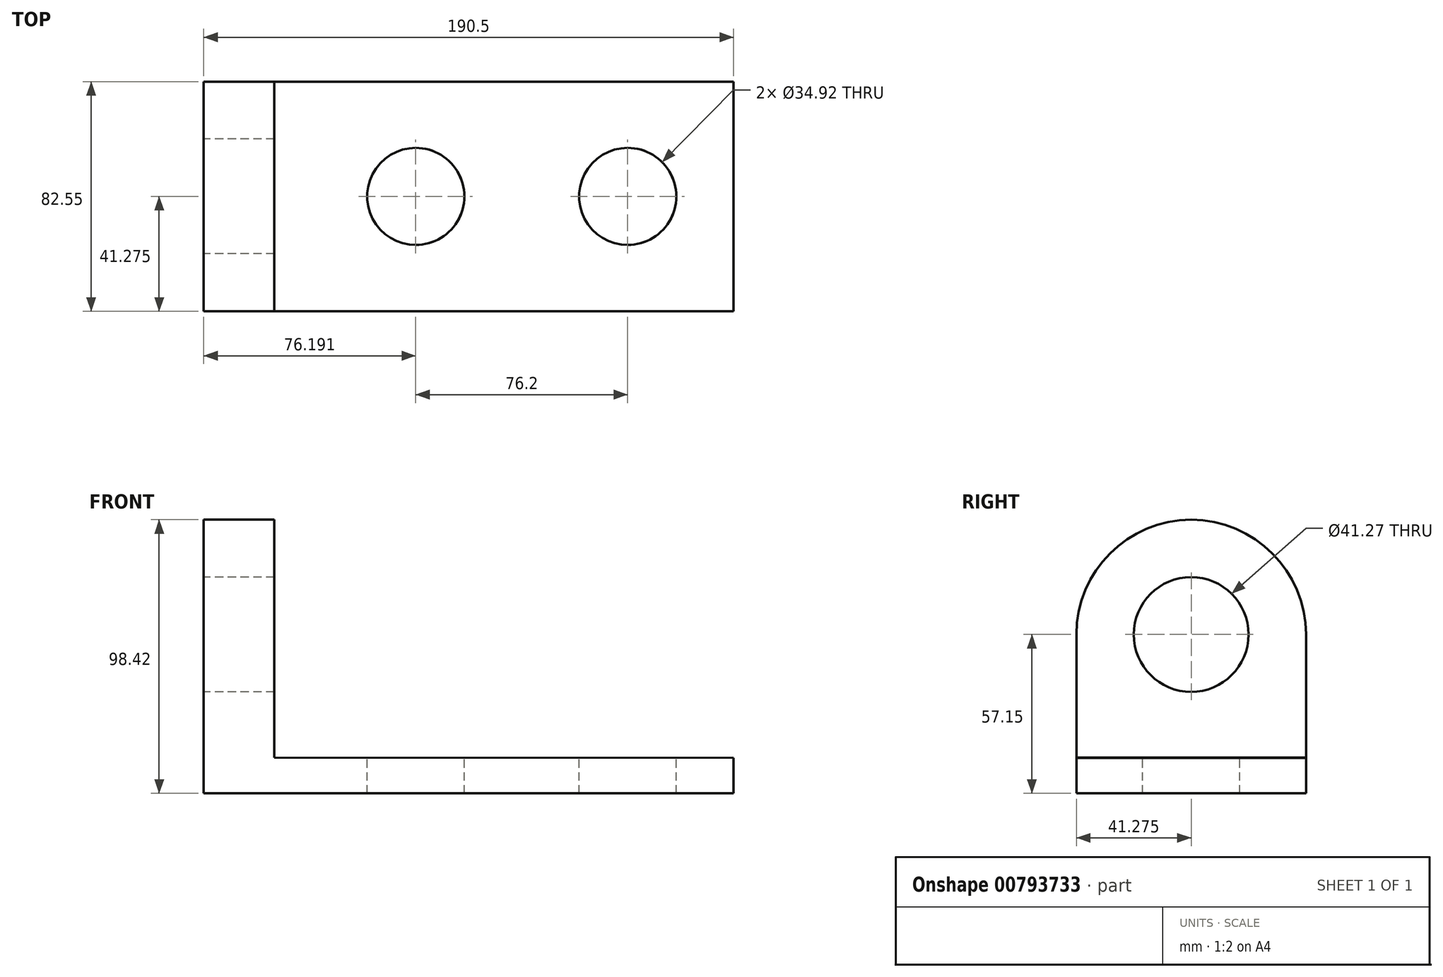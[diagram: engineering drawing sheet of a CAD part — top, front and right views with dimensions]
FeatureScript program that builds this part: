
annotation { "Feature Type Name" : "Feature", "Feature Type Description" : "" }
export const myFeature = defineFeature(function(context is Context, id is Id, definition is map)
    precondition{}
    {
        {
            var Q0;
            Q0=qCreatedBy(makeId("Front.planeOp"),FACE);
            var sketch = newSketch(context, id + "F0", { "sketchPlane" : qUnion([Q0])});
            skLineSegment(sketch, "E0", {"start": v(0, 0) * mm, "end": v(190.5, 0) * mm});
            skLineSegment(sketch, "E1", {"start": v(190.5, 0) * mm, "end": v(190.5, 12.7) * mm});
            skLineSegment(sketch, "E2", {"start": v(0, 0) * mm, "end": v(0, 114.3) * mm});
            skLineSegment(sketch, "E3", {"start": v(0, 114.3) * mm, "end": v(25.4, 114.3) * mm});
            skLineSegment(sketch, "E4", {"start": v(25.4, 114.3) * mm, "end": v(25.4, 12.92) * mm});
            skLineSegment(sketch, "E5", {"start": v(25.4, 12.92) * mm, "end": v(190.5, 12.7) * mm});
            skSolve(sketch);
        }
        {
            var Q0;
            Q0=makeQuery(id+"F0.imprint","IMPRINT",FACE,{"disambiguationData":[TD([[makeQuery(id+"F0.imprint","IMPRINT",EDGE,{"derivedFrom":sQuery(id+"F0.wireOp",EDGE,"E0")}),1.0]])]});
            extrude(context, id + "F1", {"entities" : qUnion([Q0]), "depth" : 82.55 * mm, "offsetDistance" : 25.4 * mm});
        }
        {
            var Q0;
            Q0=makeQuery(id+"F1.opExtrude","SWEPT_FACE",FACE,{"disambiguationData":[OSD([sQuery(id+"F0.wireOp",EDGE,"E2")])]});
            var sketch = newSketch(context, id + "F2", { "sketchPlane" : qUnion([Q0])});
            skLineSegment(sketch, "E6", {"start": v(0, 0) * mm, "end": v(0, 57.15) * mm});
            skLineSegment(sketch, "E7", {"start": v(82.55, 0) * mm, "end": v(82.55, 57.15) * mm});
            skArc(sketch, "E8", {"start": v(82.55, 57.15) * mm, "mid": v(41.27, 98.43) * mm, "end": v(0, 57.15) * mm});
            skCircle(sketch, "E9", {"center": v(41.27, 57.15) * mm, "radius": 20.64 * mm});
            skSolve(sketch);
        }
        {
            var Q0;
            Q0=makeQuery(id+"F2.imprint","IMPRINT",FACE,{"disambiguationData":[TD([[makeQuery(id+"F2.imprint","IMPRINT",EDGE,{"derivedFrom":sQuery(id+"F2.wireOp",EDGE,"E9")}),1.0]])]});
            var Q1;
            {var subQ0=sQuery(id+"F2.wireOp",EDGE,"E8");Q1=makeQuery(id+"F2.imprint","IMPRINT",FACE,{"disambiguationData":[TD([[makeQuery(id+"F2.imprint","IMPRINT",EDGE,{"derivedFrom":subQ0}),-1.0]])]});}
            extrude(context, id + "F3", {"entities" : qUnion([Q0, Q1]), "operationType" : NewBodyOperationType.REMOVE, "oppositeDirection" : true, "depth" : 152.4 * mm, "offsetDistance" : 25.4 * mm});
        }
        {
            var Q0;
            Q0=makeQuery(id+"F1.opExtrude","SWEPT_FACE",FACE,{"disambiguationData":[OSD([sQuery(id+"F0.wireOp",EDGE,"E5")])]});
            var sketch = newSketch(context, id + "F4", { "sketchPlane" : qUnion([Q0])});
            skLineSegment(sketch, "E10", {"start": v(190.48, -41.28) * mm, "end": v(152.38, -41.28) * mm, "construction": true});
            skLineSegment(sketch, "E11", {"start": v(152.38, -41.28) * mm, "end": v(76.18, -41.28) * mm, "construction": true});
            skCircle(sketch, "E12", {"center": v(76.18, -41.28) * mm, "radius": 17.46 * mm});
            skCircle(sketch, "E13", {"center": v(152.38, -41.28) * mm, "radius": 17.46 * mm});
            skSolve(sketch);
        }
        {
            var Q0;
            Q0=qSketchRegion(id+"F4",true);
            extrude(context, id + "F5", {"entities" : qUnion([Q0]), "operationType" : NewBodyOperationType.REMOVE, "oppositeDirection" : true, "depth" : 25.4 * mm, "offsetDistance" : 25.4 * mm});
        }
    });
